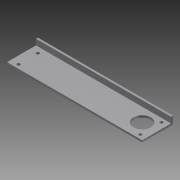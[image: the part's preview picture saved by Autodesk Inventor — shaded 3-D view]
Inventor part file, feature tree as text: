
AUTODESK INVENTOR PART (.ipt)
format: ipt  version: 2012 (Build 160160000, 160)  size: 103,424 bytes
history: native  units: in
note: dims shown in document units (in); Inventor stores cm internally (conversion verified against a paired STEP export)
features: extrude x3, sketch x2
ambient origin geometry x8: Origin, YZ Plane, XZ Plane, XY Plane, X Axis, Y Axis, Z Axis, Center Point
bodies: Solid1 (feature_tree)
feature tree (5):
  sketch  "Sketch1"  dims[d4=0.125in d6=0.125in]
  extrude  "Extrusion1"  Depth=0.125in
  extrude  "Extrusion2"  Depth=8.75in
  extrude  "Extrusion3"  Depth=0.125in TaperAngle=0.0deg
  sketch  "Sketch2"  dims[d9=0.5in d11=8.75in d14=0.125in d15=0.0in d16=2.0in d17=0.0in d22=1.0in d23=0.0in d26=1.0in d27=1.0in d28=1.125in d29=0.2in d30=0.5in d31=0.25in d32=0.5in d33=0.5in d34=0.25in d35=0.375in d36=0.375in d37=0.375in]
